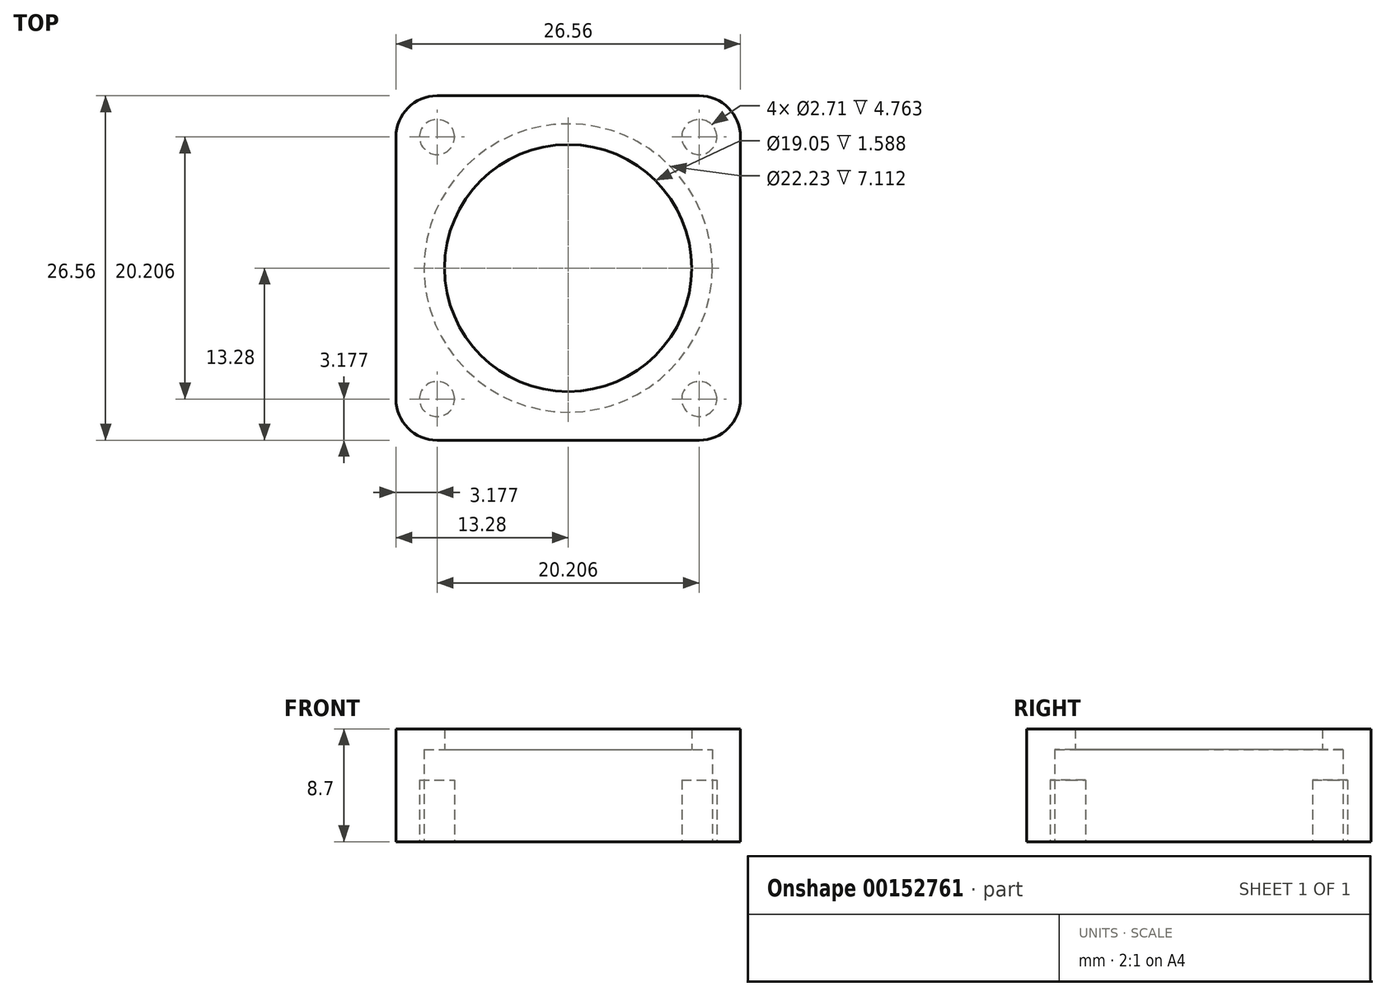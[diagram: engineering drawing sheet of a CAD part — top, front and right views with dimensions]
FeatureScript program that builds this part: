
annotation { "Feature Type Name" : "Feature", "Feature Type Description" : "" }
export const myFeature = defineFeature(function(context is Context, id is Id, definition is map)
    precondition{}
    {
        {
            var Q0;
            Q0=qCreatedBy(makeId("Top.planeOp"),FACE);
            var sketch = newSketch(context, id + "F0", { "sketchPlane" : qUnion([Q0])});
            skCircle(sketch, "E0", {"center": v(0, 0) * mm, "radius": 11.11 * mm, "construction": true});
            skLineSegment(sketch, "E1", {"start": v(0, 0) * mm, "end": v(0, -13.28) * mm, "construction": true});
            skLineSegment(sketch, "E2.bottom", {"start": v(13.28, -13.28) * mm, "end": v(-13.28, -13.28) * mm});
            skLineSegment(sketch, "E2.top", {"start": v(13.28, 13.28) * mm, "end": v(-13.28, 13.28) * mm});
            skLineSegment(sketch, "E2.left", {"start": v(13.28, -13.28) * mm, "end": v(13.28, 13.28) * mm});
            skLineSegment(sketch, "E2.right", {"start": v(-13.28, -13.28) * mm, "end": v(-13.28, 13.28) * mm});
            skLineSegment(sketch, "E3.bottom", {"start": v(-10.1, 10.1) * mm, "end": v(10.1, 10.1) * mm, "construction": true});
            skLineSegment(sketch, "E3.top", {"start": v(-10.1, -10.1) * mm, "end": v(10.1, -10.1) * mm, "construction": true});
            skLineSegment(sketch, "E3.left", {"start": v(-10.1, 10.1) * mm, "end": v(-10.1, -10.1) * mm, "construction": true});
            skLineSegment(sketch, "E3.right", {"start": v(10.1, 10.1) * mm, "end": v(10.1, -10.1) * mm, "construction": true});
            skCircle(sketch, "E4", {"center": v(-10.1, 10.1) * mm, "radius": 3.18 * mm, "construction": true});
            skLineSegment(sketch, "E5", {"start": v(0, 0) * mm, "end": v(0, 13.28) * mm, "construction": true});
            skCircle(sketch, "E6", {"center": v(-10.1, 10.1) * mm, "radius": 1.83 * mm, "construction": true});
            skCircle(sketch, "E7", {"center": v(10.1, 10.1) * mm, "radius": 1.83 * mm, "construction": true});
            skCircle(sketch, "E8", {"center": v(10.1, -10.1) * mm, "radius": 1.83 * mm, "construction": true});
            skCircle(sketch, "E9", {"center": v(-10.1, -10.1) * mm, "radius": 1.83 * mm, "construction": true});
            skCircle(sketch, "E10", {"center": v(0, 0) * mm, "radius": 9.53 * mm});
            skSolve(sketch);
        }
        {
            var Q0;
            Q0=qSketchRegion(id+"F0",true);
            extrude(context, id + "F1", {"entities" : qUnion([Q0]), "depth" : 8.7 * mm});
        }
        {
            var Q0;
            Q0=makeQuery(id+"F1.opExtrude","SWEPT_EDGE",EDGE,{"disambiguationData":[OSD([sQuery(id+"F0.wireOp",EDGE,"E2.top"),sQuery(id+"F0.wireOp",EDGE,"E2.right")])]});
            var Q1;
            Q1=makeQuery(id+"F1.opExtrude","SWEPT_EDGE",EDGE,{"disambiguationData":[OSD([sQuery(id+"F0.wireOp",EDGE,"E2.bottom"),sQuery(id+"F0.wireOp",EDGE,"E2.right")])]});
            var Q2;
            Q2=makeQuery(id+"F1.opExtrude","SWEPT_EDGE",EDGE,{"disambiguationData":[OSD([sQuery(id+"F0.wireOp",EDGE,"E2.bottom"),sQuery(id+"F0.wireOp",EDGE,"E2.left")])]});
            var Q3;
            Q3=makeQuery(id+"F1.opExtrude","SWEPT_EDGE",EDGE,{"disambiguationData":[OSD([sQuery(id+"F0.wireOp",EDGE,"E2.top"),sQuery(id+"F0.wireOp",EDGE,"E2.left")])]});
            fillet(context, id + "F2", {"entities" : qUnion([Q0, Q1, Q2, Q3]), "radius" : 3.17 * mm, "tangentPropagation" : true, "allowEdgeOverflow" : false});
        }
        {
            var Q0;
            Q0=makeQuery(id+"F1.opExtrude","CAP_FACE",FACE,{"disambiguationData":[OSD([sQuery(id+"F0.wireOp",EDGE,"E2.bottom"),sQuery(id+"F0.wireOp",EDGE,"E2.top"),sQuery(id+"F0.wireOp",EDGE,"E2.left"),sQuery(id+"F0.wireOp",EDGE,"E2.right"),sQuery(id+"F0.wireOp",EDGE,"E6"),sQuery(id+"F0.wireOp",EDGE,"E7"),sQuery(id+"F0.wireOp",EDGE,"E8"),sQuery(id+"F0.wireOp",EDGE,"E9"),sQuery(id+"F0.wireOp",EDGE,"E10")])],"isStart":true});
            var sketch = newSketch(context, id + "F3", { "sketchPlane" : qUnion([Q0])});
            skCircle(sketch, "E11", {"center": v(0, 0) * mm, "radius": 11.11 * mm});
            skSolve(sketch);
        }
        {
            var Q0;
            Q0=qSketchRegion(id+"F3",true);
            extrude(context, id + "F4", {"entities" : qUnion([Q0]), "operationType" : NewBodyOperationType.REMOVE, "oppositeDirection" : true, "depth" : 7.11 * mm});
        }
        {
            var Q0;
            Q0=makeQuery(id+"F1.opExtrude","CAP_FACE",FACE,{"disambiguationData":[OSD([sQuery(id+"F0.wireOp",EDGE,"E2.bottom"),sQuery(id+"F0.wireOp",EDGE,"E2.top"),sQuery(id+"F0.wireOp",EDGE,"E2.left"),sQuery(id+"F0.wireOp",EDGE,"E2.right"),sQuery(id+"F0.wireOp",EDGE,"E10")])],"isStart":true});
            var sketch = newSketch(context, id + "F5", { "sketchPlane" : qUnion([Q0])});
            skCircle(sketch, "E12", {"center": v(10.1, 10.1) * mm, "radius": 1.35 * mm});
            skCircle(sketch, "E13", {"center": v(-10.1, 10.1) * mm, "radius": 1.35 * mm});
            skCircle(sketch, "E14", {"center": v(-10.1, -10.1) * mm, "radius": 1.35 * mm});
            skCircle(sketch, "E15", {"center": v(10.1, -10.1) * mm, "radius": 1.35 * mm});
            skSolve(sketch);
        }
        {
            var Q0;
            Q0 = qSketchRegion(id + "F5", true);
            extrude(context, id + "F6", {"entities" : qUnion([Q0]), "operationType" : NewBodyOperationType.REMOVE, "oppositeDirection" : true, "depth" : 4.76 * mm});
        }
    });
